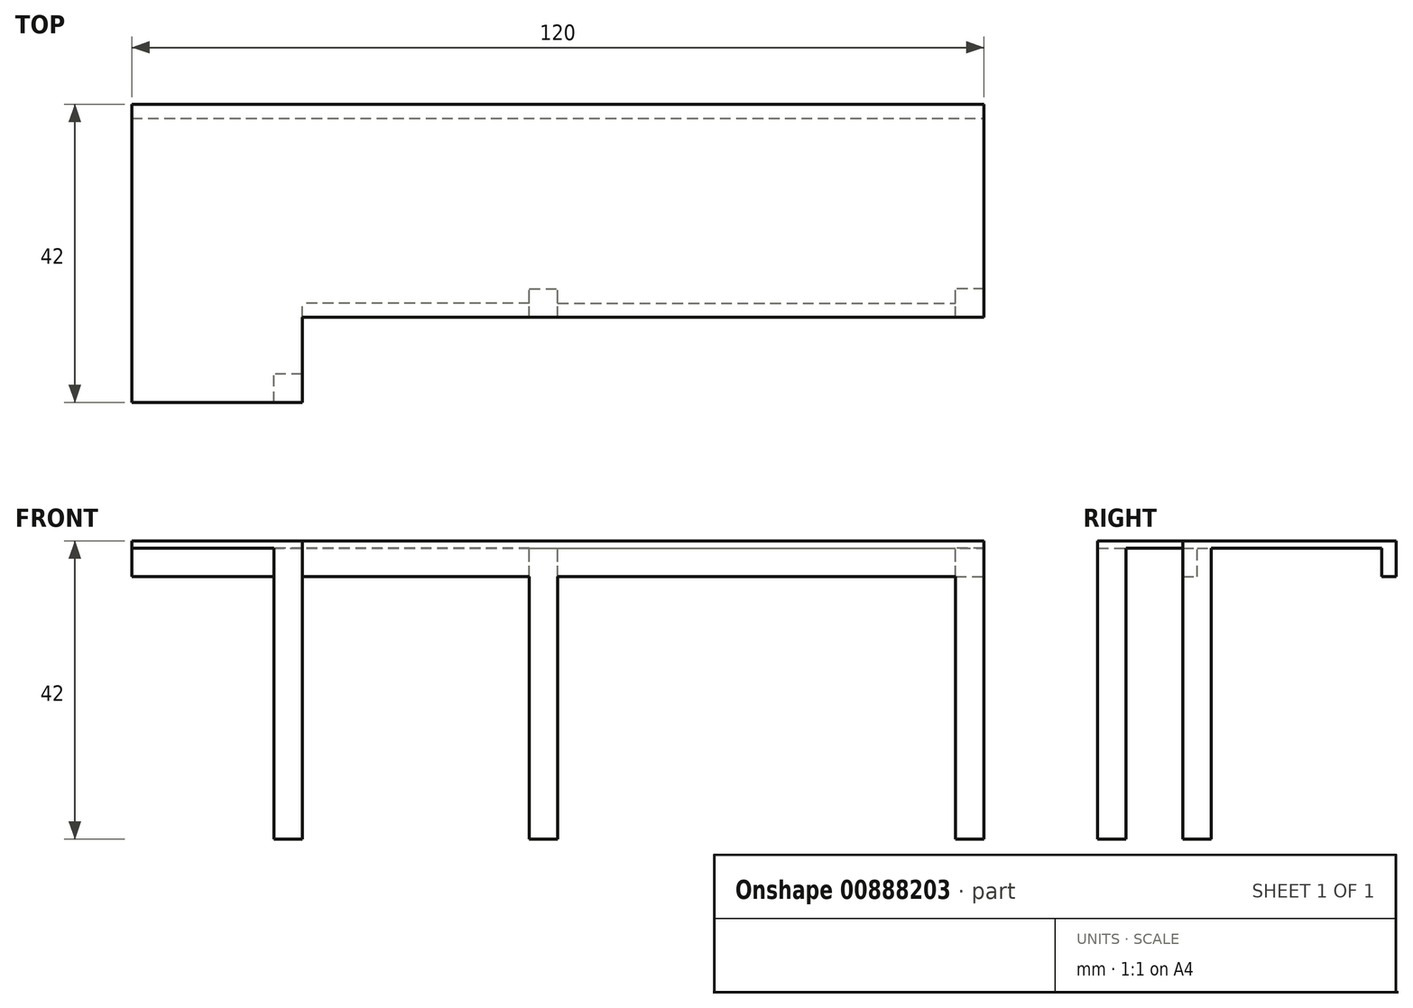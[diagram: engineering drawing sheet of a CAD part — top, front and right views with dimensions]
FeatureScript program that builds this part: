
annotation { "Feature Type Name" : "Feature", "Feature Type Description" : "" }
export const myFeature = defineFeature(function(context is Context, id is Id, definition is map)
    precondition{}
    {
        {
            var Q0;
            Q0=qCreatedBy(makeId("Top.planeOp"),FACE);
            var sketch = newSketch(context, id + "F0", { "sketchPlane" : qUnion([Q0])});
            skLineSegment(sketch, "E0", {"start": v(0, 0) * mm, "end": v(0, 42) * mm});
            skLineSegment(sketch, "E1", {"start": v(0, 42) * mm, "end": v(120, 42) * mm});
            skLineSegment(sketch, "E2", {"start": v(120, 42) * mm, "end": v(120, 12) * mm});
            skLineSegment(sketch, "E3", {"start": v(120, 12) * mm, "end": v(24, 12) * mm});
            skLineSegment(sketch, "E4", {"start": v(24, 12) * mm, "end": v(24, 0) * mm});
            skLineSegment(sketch, "E5", {"start": v(24, 0) * mm, "end": v(0, 0) * mm});
            skSolve(sketch);
        }
        {
            var Q0;
            Q0 = qSketchRegion(id + "F0", true);
            extrude(context, id + "F1", {"entities" : qUnion([Q0]), "depth" : 1 * mm, "offsetDistance" : 25 * mm});
        }
        {
            var Q0;
            Q0=makeQuery(id+"F1.opExtrude","CAP_FACE",FACE,{"disambiguationData":[OSD([sQuery(id+"F0.wireOp",EDGE,"E0"),sQuery(id+"F0.wireOp",EDGE,"E1"),sQuery(id+"F0.wireOp",EDGE,"E2"),sQuery(id+"F0.wireOp",EDGE,"E3"),sQuery(id+"F0.wireOp",EDGE,"E4"),sQuery(id+"F0.wireOp",EDGE,"E5")])],"isStart":true});
            var sketch = newSketch(context, id + "F2", { "sketchPlane" : qUnion([Q0])});
            skLineSegment(sketch, "E6.bottom", {"start": v(24, 0) * mm, "end": v(20, 0) * mm});
            skLineSegment(sketch, "E6.top", {"start": v(24, -4) * mm, "end": v(20, -4) * mm});
            skLineSegment(sketch, "E6.left", {"start": v(24, 0) * mm, "end": v(24, -4) * mm});
            skLineSegment(sketch, "E6.right", {"start": v(20, 0) * mm, "end": v(20, -4) * mm});
            skLineSegment(sketch, "E7.bottom", {"start": v(56, -12) * mm, "end": v(60, -12) * mm});
            skLineSegment(sketch, "E7.top", {"start": v(56, -16) * mm, "end": v(60, -16) * mm});
            skLineSegment(sketch, "E7.left", {"start": v(56, -12) * mm, "end": v(56, -16) * mm});
            skLineSegment(sketch, "E7.right", {"start": v(60, -12) * mm, "end": v(60, -16) * mm});
            skLineSegment(sketch, "E8.bottom", {"start": v(120, -12) * mm, "end": v(116, -12) * mm});
            skLineSegment(sketch, "E8.top", {"start": v(120, -16) * mm, "end": v(116, -16) * mm});
            skLineSegment(sketch, "E8.left", {"start": v(120, -12) * mm, "end": v(120, -16) * mm});
            skLineSegment(sketch, "E8.right", {"start": v(116, -12) * mm, "end": v(116, -16) * mm});
            skSolve(sketch);
        }
        {
            var Q0;
            Q0 = qSketchRegion(id + "F2", true);
            extrude(context, id + "F3", {"entities" : qUnion([Q0]), "operationType" : NewBodyOperationType.ADD, "depth" : 41 * mm, "offsetDistance" : 25 * mm});
        }
        {
            var Q0;
            Q0=makeQuery(id+"F1.opExtrude","CAP_FACE",FACE,{"disambiguationData":[OSD([sQuery(id+"F0.wireOp",EDGE,"E0"),sQuery(id+"F0.wireOp",EDGE,"E1"),sQuery(id+"F0.wireOp",EDGE,"E2"),sQuery(id+"F0.wireOp",EDGE,"E3"),sQuery(id+"F0.wireOp",EDGE,"E4"),sQuery(id+"F0.wireOp",EDGE,"E5")])],"isStart":true});
            var sketch = newSketch(context, id + "F4", { "sketchPlane" : qUnion([Q0])});
            skPoint(sketch, "E9.top.end.orphan", {"position": v(118, -16) * mm});
            skLineSegment(sketch, "E10.bottom", {"start": v(0, -42) * mm, "end": v(120, -42) * mm});
            skLineSegment(sketch, "E10.top", {"start": v(0, -40) * mm, "end": v(120, -40) * mm});
            skLineSegment(sketch, "E10.left", {"start": v(0, -42) * mm, "end": v(0, -40) * mm});
            skLineSegment(sketch, "E10.right", {"start": v(120, -42) * mm, "end": v(120, -40) * mm});
            skLineSegment(sketch, "E11.bottom", {"start": v(56, -12) * mm, "end": v(24, -12) * mm});
            skLineSegment(sketch, "E11.top", {"start": v(56, -14) * mm, "end": v(24, -14) * mm});
            skLineSegment(sketch, "E11.left", {"start": v(56, -12) * mm, "end": v(56, -14) * mm});
            skLineSegment(sketch, "E11.right", {"start": v(24, -12) * mm, "end": v(24, -14) * mm});
            skLineSegment(sketch, "E12.bottom", {"start": v(60, -12) * mm, "end": v(116, -12) * mm});
            skLineSegment(sketch, "E12.top", {"start": v(60, -14) * mm, "end": v(116, -14) * mm});
            skLineSegment(sketch, "E12.left", {"start": v(60, -12) * mm, "end": v(60, -14) * mm});
            skLineSegment(sketch, "E12.right", {"start": v(116, -12) * mm, "end": v(116, -14) * mm});
            skSolve(sketch);
        }
        {
            var Q0;
            Q0 = qSketchRegion(id + "F4", true);
            extrude(context, id + "F5", {"entities" : qUnion([Q0]), "operationType" : NewBodyOperationType.ADD, "depth" : 4 * mm, "offsetDistance" : 25 * mm});
        }
    });
